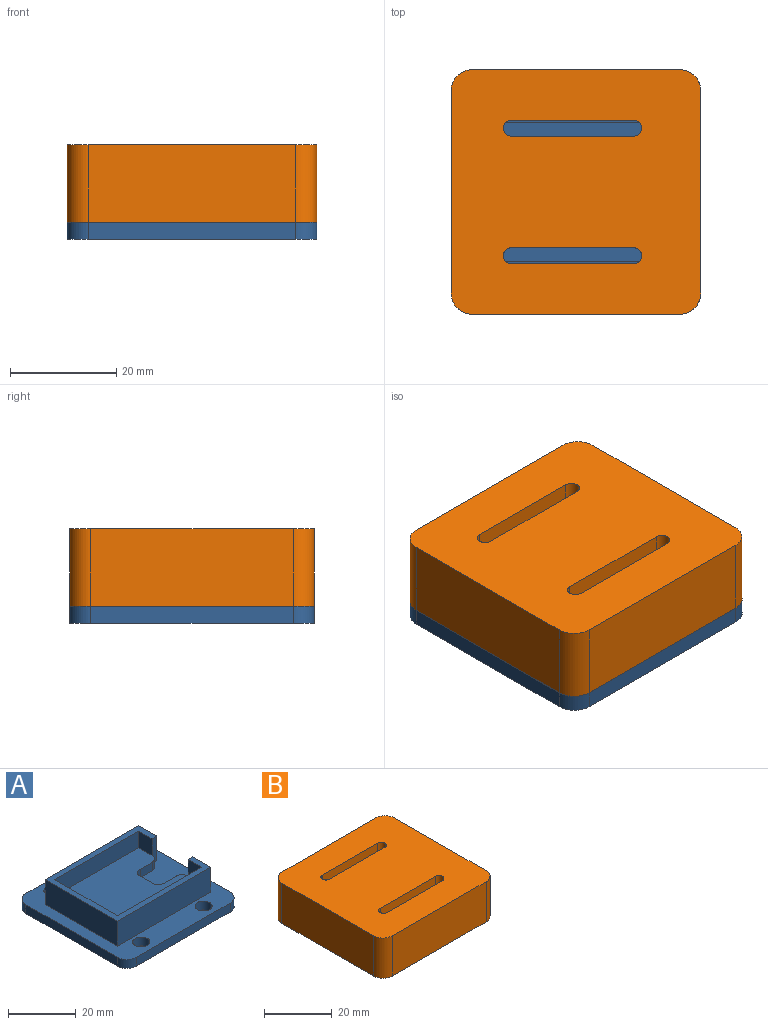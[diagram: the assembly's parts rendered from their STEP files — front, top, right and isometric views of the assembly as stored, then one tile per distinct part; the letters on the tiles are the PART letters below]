
ASSEMBLY  parts=2 mates=1
PART A: 35 faces, bbox 47x46x12.2 mm
  f0: plane 5x3mm, normal (0,-1,0), area 15mm2, adj f1,f6,f7,f21
  f1: cylinder r=2.5mm len=3mm, axis (0,0,-1), area 11.8mm2, adj f0,f7,f15,f21
  f2: cylinder r=2.5mm len=3mm, axis (0,0,-1), area 11.8mm2, adj f3,f7,f14,f21
  f3: plane 5x3mm, normal (0,1,0), area 15mm2, adj f2,f4,f7,f21
  f4: cylinder r=2.5mm len=3mm, axis (0,0,-1), area 11.8mm2, adj f3,f5,f7,f21
  f5: plane 5x3mm, normal (1,0,0), area 15mm2, adj f4,f6,f7,f21
  f6: cylinder r=2.5mm len=3mm, axis (0,0,-1), area 11.8mm2, adj f0,f5,f7,f21
  f7: plane 35x26mm, normal (0,0,1), area 810mm2, adj f0,f1,f2,f3,f4,f5,f6,f8
  f8: plane 35x6mm, normal (0,-1,0), area 210mm2, adj f7,f9,f11,f20
  f9: plane 26x6mm, normal (1,0,0), area 156mm2, adj f7,f8,f10,f20
  f10: plane 35x6mm, normal (0,1,0), area 210mm2, adj f7,f9,f12,f20
  f11: plane 6x5.5mm, normal (-1,0,0), area 33mm2, adj f7,f8,f15,f20
  f12: plane 6x5.5mm, normal (-1,0,0), area 33mm2, adj f7,f10,f14,f20
  f13: plane 9x7.5mm, normal (1,0,0), area 67.5mm2, adj f14,f19,f20,f21
  f14: plane 9x2mm, normal (0,1,0), area 18mm2, adj f2,f12,f13,f20,f21
  f15: plane 9x2mm, normal (0,-1,0), area 18mm2, adj f1,f11,f16,f20,f21
  f16: plane 9x7.5mm, normal (1,0,0), area 67.5mm2, adj f15,f17,f20,f21
  f17: plane 39x9mm, normal (0,1,0), area 351mm2, adj f16,f18,f20,f21
  f18: plane 30x9mm, normal (-1,0,0), area 270mm2, adj f17,f19,f20,f21
  f19: plane 39x9mm, normal (0,-1,0), area 351mm2, adj f13,f18,f20,f21
  f20: plane 39x30mm, normal (0,0,1), area 230mm2, adj f8,f9,f10,f11,f12,f13,f14,f15
  f21: plane 47x46mm, normal (0,0,1), area 1028.1mm2, adj f0,f1,f2,f3,f4,f5,f6,f13
  f22: plane 39x3.2mm, normal (0,1,0), area 124.8mm2, adj f21,f23,f33,f34
  f23: cylinder r=4mm len=4mm, axis (0,0,1), area 20.1mm2, adj f21,f22,f24,f34
  f24: plane 38x3.2mm, normal (-1,0,0), area 121.6mm2, adj f21,f23,f25,f34
  f25: cylinder r=4mm len=4mm, axis (0,0,1), area 20.1mm2, adj f21,f24,f26,f34
  f26: plane 39x3.2mm, normal (0,-1,0), area 124.8mm2, adj f21,f25,f27,f34
  f27: cylinder r=4mm len=4mm, axis (0,0,1), area 20.1mm2, adj f21,f26,f28,f34
  f28: plane 38x3.2mm, normal (1,0,0), area 121.6mm2, adj f21,f27,f33,f34
  f29: cylinder r=2.52mm len=5.05mm, axis (0,0,1), area 50.8mm2, adj f21,f34
  f30: cylinder r=2.52mm len=5.05mm, axis (0,0,1), area 50.8mm2, adj f21,f34
  f31: cylinder r=2.52mm len=5.05mm, axis (0,0,1), area 50.8mm2, adj f21,f34
  f32: cylinder r=2.52mm len=5.05mm, axis (0,0,1), area 50.8mm2, adj f21,f34
  f33: cylinder r=4mm len=4mm, axis (0,0,1), area 20.1mm2, adj f21,f22,f28,f34
  f34: plane 47x46mm, normal (0,0,-1), area 2068.1mm2, adj f22,f23,f24,f25,f26,f27,f28,f29
PART B: 36 faces, bbox 47x46x14.5 mm
  f0: plane 39.3x9.5mm, normal (0,-1,0), area 373.4mm2, adj f1,f14,f15,f16
  f1: plane 10.15x9.5mm, normal (-1,0,0), area 74mm2, adj f0,f2,f15,f16,f27
  f2: plane 7x3.85mm, normal (0,-1,0), area 27mm2, adj f1,f10,f15,f27
  f3: cylinder r=4mm len=14.5mm, axis (0,0,-1), area 91.1mm2, adj f4,f10,f15,f21
  f4: plane 39x14.5mm, normal (0,1,0), area 565.5mm2, adj f3,f5,f15,f21
  f5: cylinder r=4mm len=14.5mm, axis (0,0,-1), area 91.1mm2, adj f4,f6,f15,f21
  f6: plane 38x14.5mm, normal (-1,0,0), area 551mm2, adj f5,f7,f15,f21
  f7: cylinder r=4mm len=14.5mm, axis (0,0,-1), area 91.1mm2, adj f6,f8,f15,f21
  f8: plane 39x14.5mm, normal (0,-1,0), area 565.5mm2, adj f7,f9,f15,f21
  f9: cylinder r=4mm len=14.5mm, axis (0,0,-1), area 91.1mm2, adj f8,f10,f15,f21
  f10: plane 38x14.5mm, normal (1,0,0), area 411.2mm2, adj f2,f3,f9,f11,f15,f16,f21,f26
  f11: plane 7x3.85mm, normal (0,1,0), area 27mm2, adj f10,f12,f15,f26
  f12: plane 10.15x9.5mm, normal (-1,0,0), area 74mm2, adj f11,f13,f15,f16,f26
  f13: plane 39.3x9.5mm, normal (0,1,0), area 373.4mm2, adj f12,f14,f15,f16
  f14: plane 30.3x9.5mm, normal (1,0,0), area 287.9mm2, adj f0,f13,f15,f16
  f15: plane 47x46mm, normal (0,0,-1), area 819.6mm2, adj f0,f1,f2,f3,f4,f5,f6,f7
  f16: plane 43.15x30.3mm, normal (0,0,-1), area 1077.2mm2, adj f0,f1,f10,f12,f13,f14,f17,f18
  f17: plane 23x5mm, normal (0,-1,0), area 115mm2, adj f16,f21,f22,f23
  f18: plane 23x5mm, normal (0,1,0), area 115mm2, adj f16,f21,f24,f25
  f19: plane 23x5mm, normal (0,-1,0), area 115mm2, adj f16,f21,f24,f25
  f20: plane 23x5mm, normal (0,1,0), area 115mm2, adj f16,f21,f22,f23
  f21: plane 47x46mm, normal (0,0,1), area 1996.1mm2, adj f3,f4,f5,f6,f7,f8,f9,f10
  f22: cylinder r=1.5mm len=5mm, axis (0,0,-1), area 23.6mm2, adj f16,f17,f20,f21
  f23: cylinder r=1.5mm len=5mm, axis (0,0,1), area 23.6mm2, adj f16,f17,f20,f21
  f24: cylinder r=1.5mm len=5mm, axis (0,0,-1), area 23.6mm2, adj f16,f18,f19,f21
  f25: cylinder r=1.5mm len=5mm, axis (0,0,1), area 23.6mm2, adj f16,f18,f19,f21
  f26: cylinder r=2.5mm len=3.85mm, axis (1,0,0), area 15.1mm2, adj f10,f11,f12,f16
  f27: cylinder r=2.5mm len=3.85mm, axis (-1,0,0), area 15.1mm2, adj f1,f2,f10,f16
  f28: cylinder r=2.52mm len=5.05mm, axis (0,0,-1), area 63.5mm2, adj f15,f29
  f29: plane 5.05x5.05mm, normal (0,0,-1), area 20mm2, adj f28
  f30: cylinder r=2.52mm len=5.05mm, axis (0,0,-1), area 63.5mm2, adj f15,f31
  f31: plane 5.05x5.05mm, normal (0,0,-1), area 20mm2, adj f30
  f32: cylinder r=2.52mm len=5.05mm, axis (0,0,-1), area 63.5mm2, adj f15,f33
  f33: plane 5.05x5.05mm, normal (0,0,-1), area 20mm2, adj f32
  f34: cylinder r=2.52mm len=5.05mm, axis (0,0,-1), area 63.5mm2, adj f15,f35
  f35: plane 5.05x5.05mm, normal (0,0,-1), area 20mm2, adj f34
PLACE A t=(-48.77,-70.72,20.04)mm
PLACE B t=(-127.1,-63.33,20.04)mm
MATE slider A.f29 <-> B.f30  axis (0,0,1) through (-30.43,-68.23,20.04)mm
